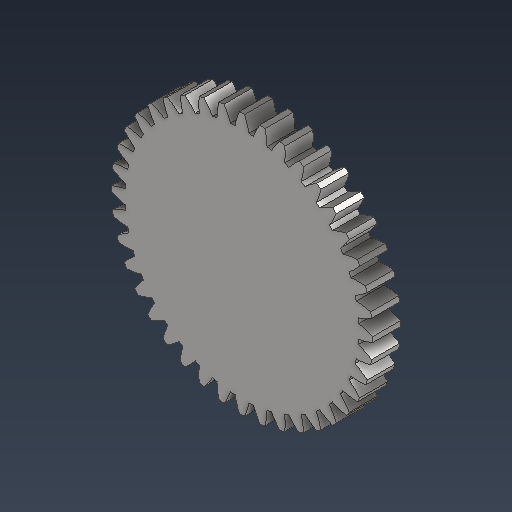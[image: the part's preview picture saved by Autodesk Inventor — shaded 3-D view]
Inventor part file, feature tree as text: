
AUTODESK INVENTOR PART (.ipt)
format: ipt  version: 2021 (Build 250183000, 183)  size: 316,928 bytes
history: native  units: mm (DEFAULTED — no unit token found)
features: plane x3, other x3, sketch x2, extrude x1
ambient origin geometry x8: Origin, YZ Plane, XZ Plane, XY Plane, X Axis, Y Axis, Z Axis, Center Point
bodies: Solid1 (feature_tree)
feature tree (9):
  extrude  "Extrusion1"  Depth=0.5mm TaperAngle=0.0deg
  plane  "Work Plane2"
  plane  "Work Plane8"
  plane  "Work Plane9"
  other  "Engrenagem reta"
  sketch  "Sketch1"  dims[d0=4.666mm d1=0.5mm d2=0.0mm]
  sketch  "Sketch2"  dims[d3=4.4mm d4=10.0mm d5=0.0mm d16=3.598mm d17=0.0mm d34=0.785398mm d39=0.0mm d41=0.0mm d43=3.598mm d46=3.598mm d47=0.0mm d48=0.0mm]
  other  "Srf1"
  other  "Diâmetro do flanco"
